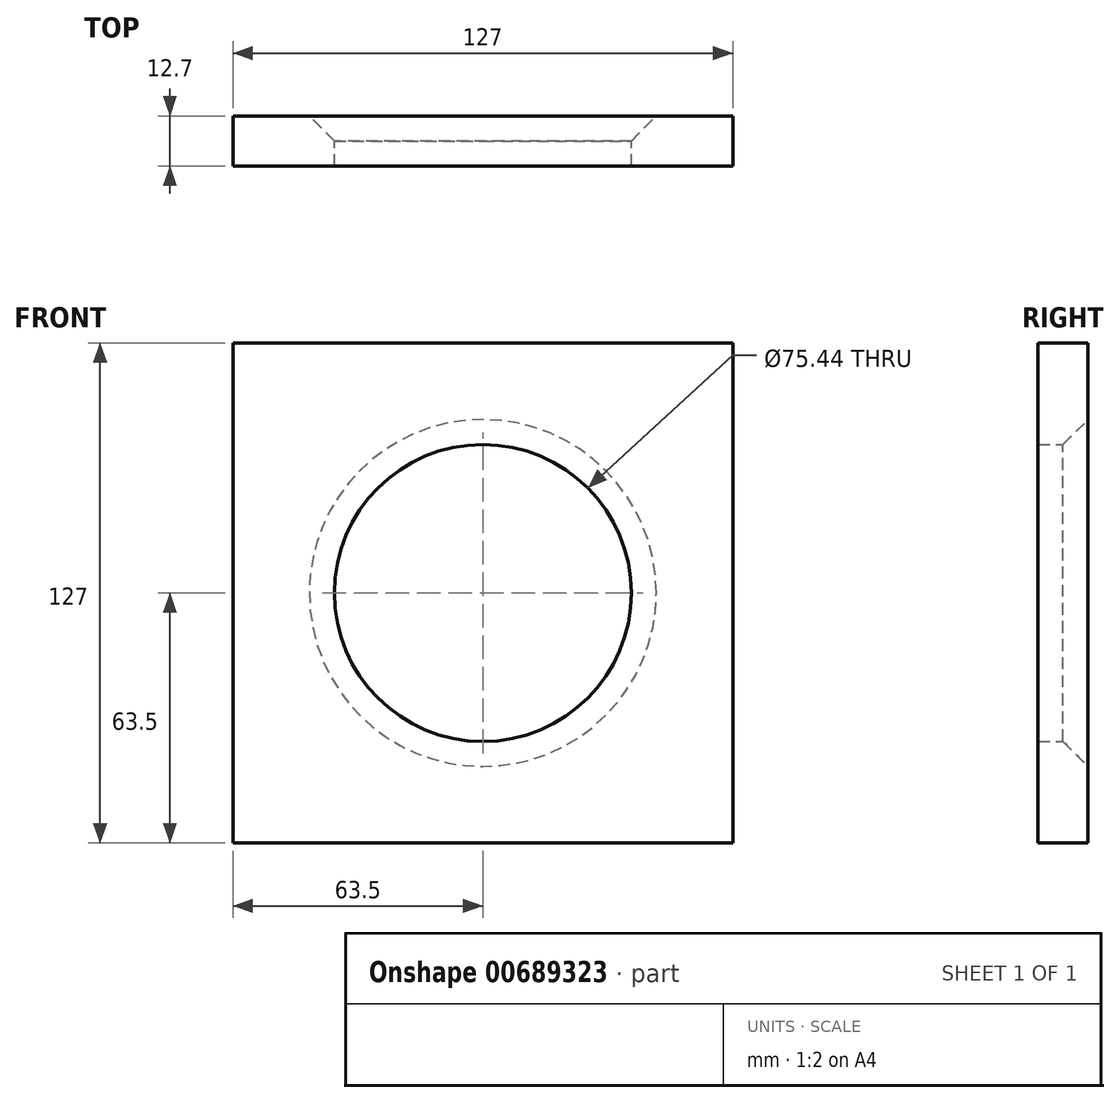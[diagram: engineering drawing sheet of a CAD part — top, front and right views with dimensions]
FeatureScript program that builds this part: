
annotation { "Feature Type Name" : "Feature", "Feature Type Description" : "" }
export const myFeature = defineFeature(function(context is Context, id is Id, definition is map)
    precondition{}
    {
        {
            var Q0;
            Q0=qCreatedBy(makeId("Front.planeOp"),FACE);
            var sketch = newSketch(context, id + "F0", { "sketchPlane" : qUnion([Q0])});
            skLineSegment(sketch, "E0.bottom", {"start": v(-63.5, 63.5) * mm, "end": v(63.5, 63.5) * mm});
            skLineSegment(sketch, "E0.top", {"start": v(-63.5, -63.5) * mm, "end": v(63.5, -63.5) * mm});
            skLineSegment(sketch, "E0.left", {"start": v(-63.5, 63.5) * mm, "end": v(-63.5, -63.5) * mm});
            skLineSegment(sketch, "E0.right", {"start": v(63.5, 63.5) * mm, "end": v(63.5, -63.5) * mm});
            skPoint(sketch, "E0.middle", {"position": v(0, 0) * mm});
            skCircle(sketch, "E1", {"center": v(0, 0) * mm, "radius": 37.72 * mm});
            skSolve(sketch);
        }
        {
            var Q0;
            Q0 = qSketchRegion(id + "F0", true);
            extrude(context, id + "F1", {"entities" : qUnion([Q0]), "depth" : 12.7 * mm, "offsetDistance" : 25.4 * mm});
        }
        {
            var Q0;
            Q0=makeQuery(id+"F1.opExtrude","CAP_EDGE",EDGE,{"disambiguationData":[OSD([sQuery(id+"F0.wireOp",EDGE,"E1")])],"isStart":true});
            chamfer(context, id + "F2", {"entities" : qUnion([Q0]), "chamferType" : ChamferType.OFFSET_ANGLE, "width" : 6.35 * mm, "oppositeDirection" : false, "angle" : 45 * degree, "tangentPropagation" : true});
        }
    });
